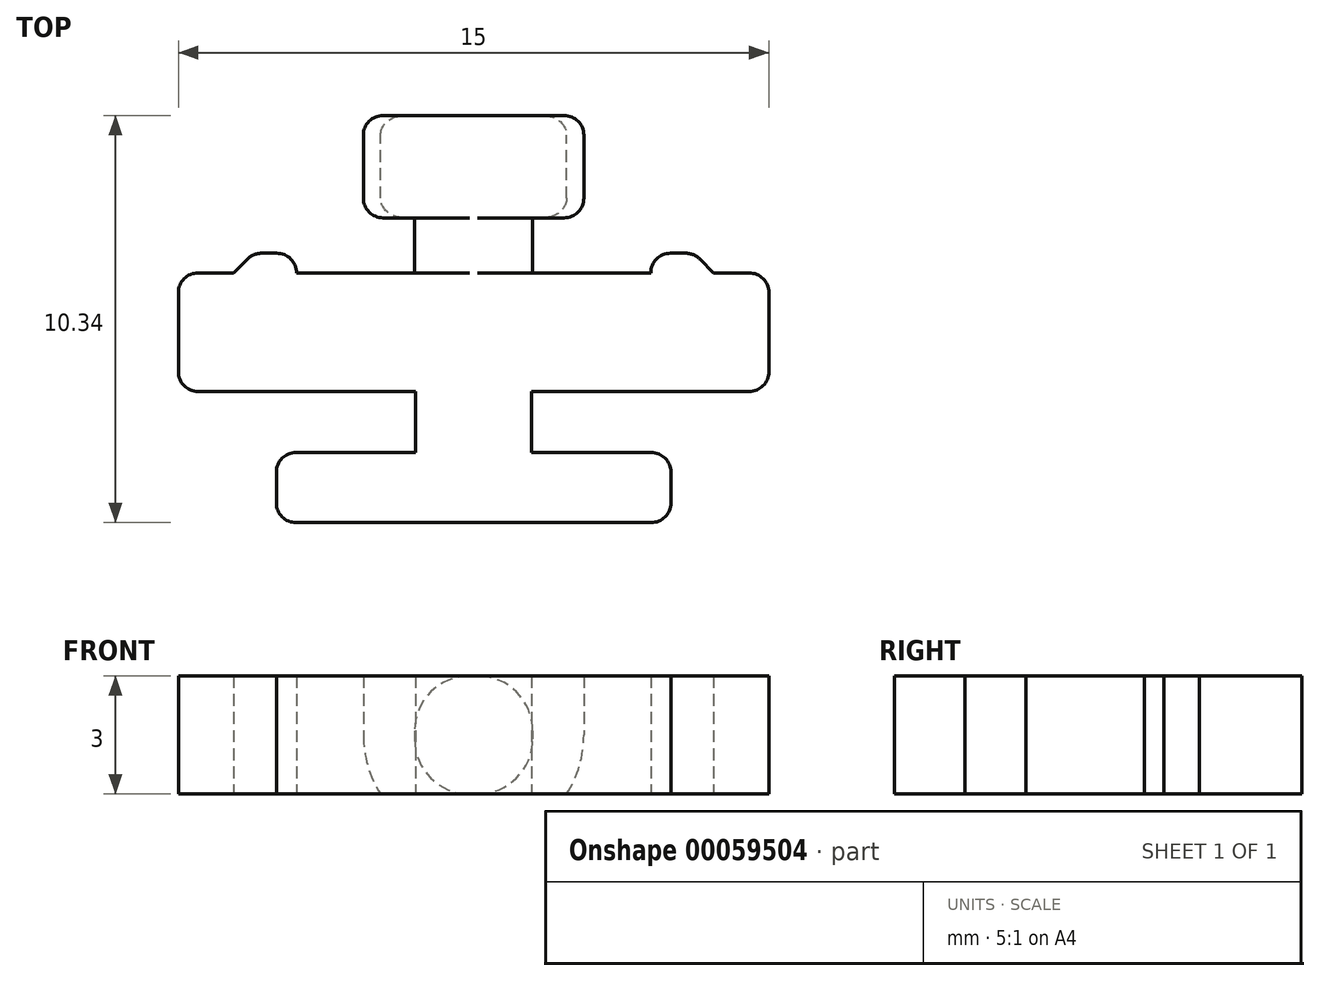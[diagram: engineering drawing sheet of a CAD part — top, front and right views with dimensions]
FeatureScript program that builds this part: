
annotation { "Feature Type Name" : "Feature", "Feature Type Description" : "" }
export const myFeature = defineFeature(function(context is Context, id is Id, definition is map)
    precondition{}
    {
        {
            assignVariable(context, id + "F0", {"name" : "SlotW", "anyValue" : 3});
        }
        {
            var Q0;
            Q0=qCreatedBy(makeId("Top.planeOp"),FACE);
            var sketch = newSketch(context, id + "F1", { "sketchPlane" : qUnion([Q0])});
            skLineSegment(sketch, "E0", {"start": v(2.8, 4) * mm, "end": v(2.8, 1.4) * mm});
            skLineSegment(sketch, "E1", {"start": v(2.8, 1.4) * mm, "end": v(1.5, 1.4) * mm});
            skLineSegment(sketch, "E2", {"start": v(1.5, 1.4) * mm, "end": v(1.5, 0) * mm});
            skLineSegment(sketch, "E3", {"start": v(1.5, 0) * mm, "end": v(4.5, 0) * mm});
            skLineSegment(sketch, "E4", {"start": v(4.5, 0) * mm, "end": v(4.5, 0.5) * mm});
            skLineSegment(sketch, "E5", {"start": v(4.5, 0.5) * mm, "end": v(5.6, 0.5) * mm});
            skLineSegment(sketch, "E6", {"start": v(5.6, 0.5) * mm, "end": v(6.1, 0) * mm});
            skLineSegment(sketch, "E7", {"start": v(6.1, 0) * mm, "end": v(7.5, 0) * mm});
            skLineSegment(sketch, "E8", {"start": v(7.5, 0) * mm, "end": v(7.5, -3.01) * mm});
            skLineSegment(sketch, "E9", {"start": v(7.5, -3.01) * mm, "end": v(1.47, -3.01) * mm});
            skLineSegment(sketch, "E10", {"start": v(1.47, -3.01) * mm, "end": v(1.47, -4.56) * mm});
            skLineSegment(sketch, "E11", {"start": v(1.47, -4.56) * mm, "end": v(5.01, -4.56) * mm});
            skLineSegment(sketch, "E12", {"start": v(5.01, -4.56) * mm, "end": v(5.01, -6.34) * mm});
            skLineSegment(sketch, "E13.MirrorCS", {"start": v(-4.5, 0.5) * mm, "end": v(-5.6, 0.5) * mm});
            skLineSegment(sketch, "E14.MirrorCS", {"start": v(-2.8, 4) * mm, "end": v(-2.8, 1.4) * mm});
            skLineSegment(sketch, "E15.MirrorCS", {"start": v(-2.8, 1.4) * mm, "end": v(-1.5, 1.4) * mm});
            skLineSegment(sketch, "E16.MirrorCS", {"start": v(-5.01, -4.56) * mm, "end": v(-5.01, -6.34) * mm});
            skLineSegment(sketch, "E17.MirrorCS", {"start": v(-1.47, -4.56) * mm, "end": v(-5.01, -4.56) * mm});
            skLineSegment(sketch, "E18.MirrorCS", {"start": v(-1.47, -3.01) * mm, "end": v(-1.47, -4.56) * mm});
            skLineSegment(sketch, "E19.MirrorCS", {"start": v(-1.5, 1.4) * mm, "end": v(-1.5, 0) * mm});
            skLineSegment(sketch, "E20.MirrorCS", {"start": v(-1.5, 0) * mm, "end": v(-4.5, 0) * mm});
            skLineSegment(sketch, "E21.MirrorCS", {"start": v(-5.6, 0.5) * mm, "end": v(-6.1, 0) * mm});
            skLineSegment(sketch, "E22.MirrorCS", {"start": v(-7.5, -3.01) * mm, "end": v(-1.47, -3.01) * mm});
            skLineSegment(sketch, "E23.MirrorCS", {"start": v(-6.1, 0) * mm, "end": v(-7.5, 0) * mm});
            skLineSegment(sketch, "E24.MirrorCS", {"start": v(-7.5, 0) * mm, "end": v(-7.5, -3.01) * mm});
            skLineSegment(sketch, "E25.MirrorCS", {"start": v(-4.5, 0) * mm, "end": v(-4.5, 0.5) * mm});
            skLineSegment(sketch, "E26", {"start": v(-2.8, 4) * mm, "end": v(2.8, 4) * mm});
            skLineSegment(sketch, "E27", {"start": v(-5.01, -6.34) * mm, "end": v(5.01, -6.34) * mm});
            skSolve(sketch);
        }
        {
            var Q0;
            Q0=makeQuery(id+"F1.imprint","IMPRINT",FACE,{"disambiguationData":[TD([[makeQuery(id+"F1.imprint","IMPRINT",EDGE,{"derivedFrom":sQuery(id+"F1.wireOp",EDGE,"E0")}),-1.0]])]});
            extrude(context, id + "F2", {"entities" : qUnion([Q0]), "depth" : (getVariable(context, 'SlotW')) * mm});
        }
        {
            var Q0;
            Q0=makeQuery(id+"F2.opExtrude","SWEPT_FACE",FACE,{"disambiguationData":[OSD([sQuery(id+"F1.wireOp",EDGE,"E26")])]});
            var sketch = newSketch(context, id + "F3", { "sketchPlane" : qUnion([Q0])});
            skCircle(sketch, "E28", {"center": v(0, 1.5) * mm, "radius": 2.8 * mm});
            skPoint(sketch, "E28.centerSnap0", {"position": v(2.8, 1.5) * mm});
            skSolve(sketch);
        }
        {
            var Q0;
            {var subQ0=sQuery(id+"F3.wireOp",EDGE,"E28");var subQ1=sQuery(id+"F1.wireOp",EDGE,"E26");var subQ2=makeQuery(id+"F2.opExtrude","CAP_EDGE",EDGE,{"disambiguationData":[OSD([subQ1])],"isStart":false});var subQ3=makeQuery(id+"F3.imprint","INTERSECT",VERTEX,{"disambiguationData":[OD(1.0)],"derivedFrom":[subQ2,subQ0]});Q0=makeQuery(id+"F3.imprint","IMPRINT",FACE,{"disambiguationData":[TD([[makeQuery(id+"F3.imprint","IMPRINT",EDGE,{"disambiguationData":[TD([[subQ3,-1.0]])],"derivedFrom":subQ0}),-1.0]])]});}
            var Q1;
            {var subQ0=sQuery(id+"F3.wireOp",EDGE,"E28");var subQ1=sQuery(id+"F1.wireOp",EDGE,"E26");var subQ2=makeQuery(id+"F2.opExtrude","CAP_EDGE",EDGE,{"disambiguationData":[OSD([subQ1])],"isStart":false});var subQ3=makeQuery(id+"F3.imprint","INTERSECT",VERTEX,{"disambiguationData":[OD(0.0)],"derivedFrom":[subQ2,subQ0]});Q1=makeQuery(id+"F3.imprint","IMPRINT",FACE,{"disambiguationData":[TD([[makeQuery(id+"F3.imprint","IMPRINT",EDGE,{"disambiguationData":[TD([[subQ3,1.0]])],"derivedFrom":subQ0}),-1.0]])]});}
            var Q2;
            {var subQ0=sQuery(id+"F3.wireOp",EDGE,"E28");var subQ1=sQuery(id+"F1.wireOp",EDGE,"E26");var subQ4=makeQuery(id+"F2.opExtrude","CAP_EDGE",EDGE,{"disambiguationData":[OSD([subQ1])],"isStart":true});var subQ5=makeQuery(id+"F3.imprint","INTERSECT",VERTEX,{"disambiguationData":[OD(1.0)],"derivedFrom":[subQ4,subQ0]});Q2=makeQuery(id+"F3.imprint","IMPRINT",FACE,{"disambiguationData":[TD([[makeQuery(id+"F3.imprint","IMPRINT",EDGE,{"disambiguationData":[TD([[subQ5,-1.0]])],"derivedFrom":subQ0}),-1.0]])]});}
            var Q3;
            {var subQ0=sQuery(id+"F3.wireOp",EDGE,"E28");var subQ1=sQuery(id+"F1.wireOp",EDGE,"E26");var subQ4=makeQuery(id+"F2.opExtrude","CAP_EDGE",EDGE,{"disambiguationData":[OSD([subQ1])],"isStart":true});var subQ5=makeQuery(id+"F3.imprint","INTERSECT",VERTEX,{"disambiguationData":[OD(0.0)],"derivedFrom":[subQ4,subQ0]});Q3=makeQuery(id+"F3.imprint","IMPRINT",FACE,{"disambiguationData":[TD([[makeQuery(id+"F3.imprint","IMPRINT",EDGE,{"disambiguationData":[TD([[subQ5,1.0]])],"derivedFrom":subQ0}),-1.0]])]});}
            extrude(context, id + "F4", {"entities" : qUnion([Q0, Q1, Q2, Q3]), "operationType" : NewBodyOperationType.REMOVE, "endBound" : BoundingType.UP_TO_NEXT, "oppositeDirection" : true, "depth" : 25 * mm});
        }
        {
            var Q0;
            Q0=makeQuery(id+"F2.opExtrude","SWEPT_EDGE",EDGE,{"disambiguationData":[OSD([sQuery(id+"F1.wireOp",EDGE,"E0"),sQuery(id+"F1.wireOp",EDGE,"E26")])]});
            var Q1;
            Q1=makeQuery(id+"F2.opExtrude","SWEPT_EDGE",EDGE,{"disambiguationData":[OSD([sQuery(id+"F1.wireOp",EDGE,"E14.MirrorCS"),sQuery(id+"F1.wireOp",EDGE,"E26")])]});
            var Q2;
            Q2=makeQuery(id+"F2.opExtrude","SWEPT_EDGE",EDGE,{"disambiguationData":[OSD([sQuery(id+"F1.wireOp",EDGE,"E4"),sQuery(id+"F1.wireOp",EDGE,"E5")])]});
            var Q3;
            Q3=makeQuery(id+"F2.opExtrude","SWEPT_EDGE",EDGE,{"disambiguationData":[OSD([sQuery(id+"F1.wireOp",EDGE,"E5"),sQuery(id+"F1.wireOp",EDGE,"E6")])]});
            var Q4;
            Q4=makeQuery(id+"F2.opExtrude","SWEPT_EDGE",EDGE,{"disambiguationData":[OSD([sQuery(id+"F1.wireOp",EDGE,"E7"),sQuery(id+"F1.wireOp",EDGE,"E8")])]});
            var Q5;
            Q5=makeQuery(id+"F2.opExtrude","SWEPT_EDGE",EDGE,{"disambiguationData":[OSD([sQuery(id+"F1.wireOp",EDGE,"E8"),sQuery(id+"F1.wireOp",EDGE,"E9")])]});
            var Q6;
            Q6=makeQuery(id+"F2.opExtrude","SWEPT_EDGE",EDGE,{"disambiguationData":[OSD([sQuery(id+"F1.wireOp",EDGE,"E11"),sQuery(id+"F1.wireOp",EDGE,"E12")])]});
            var Q7;
            Q7=makeQuery(id+"F2.opExtrude","SWEPT_EDGE",EDGE,{"disambiguationData":[OSD([sQuery(id+"F1.wireOp",EDGE,"E12"),sQuery(id+"F1.wireOp",EDGE,"E27")])]});
            var Q8;
            Q8=makeQuery(id+"F2.opExtrude","SWEPT_EDGE",EDGE,{"disambiguationData":[OSD([sQuery(id+"F1.wireOp",EDGE,"E0"),sQuery(id+"F1.wireOp",EDGE,"E1")])]});
            var Q9;
            Q9=makeQuery(id+"F2.opExtrude","SWEPT_EDGE",EDGE,{"disambiguationData":[OSD([sQuery(id+"F1.wireOp",EDGE,"E14.MirrorCS"),sQuery(id+"F1.wireOp",EDGE,"E15.MirrorCS")])]});
            var Q10;
            Q10=makeQuery(id+"F2.opExtrude","SWEPT_EDGE",EDGE,{"disambiguationData":[OSD([sQuery(id+"F1.wireOp",EDGE,"E13.MirrorCS"),sQuery(id+"F1.wireOp",EDGE,"E25.MirrorCS")])]});
            var Q11;
            Q11=makeQuery(id+"F2.opExtrude","SWEPT_EDGE",EDGE,{"disambiguationData":[OSD([sQuery(id+"F1.wireOp",EDGE,"E13.MirrorCS"),sQuery(id+"F1.wireOp",EDGE,"E21.MirrorCS")])]});
            var Q12;
            Q12=makeQuery(id+"F2.opExtrude","SWEPT_EDGE",EDGE,{"disambiguationData":[OSD([sQuery(id+"F1.wireOp",EDGE,"E23.MirrorCS"),sQuery(id+"F1.wireOp",EDGE,"E24.MirrorCS")])]});
            var Q13;
            Q13=makeQuery(id+"F2.opExtrude","SWEPT_EDGE",EDGE,{"disambiguationData":[OSD([sQuery(id+"F1.wireOp",EDGE,"E22.MirrorCS"),sQuery(id+"F1.wireOp",EDGE,"E24.MirrorCS")])]});
            var Q14;
            Q14=makeQuery(id+"F2.opExtrude","SWEPT_EDGE",EDGE,{"disambiguationData":[OSD([sQuery(id+"F1.wireOp",EDGE,"E16.MirrorCS"),sQuery(id+"F1.wireOp",EDGE,"E27")])]});
            var Q15;
            Q15=makeQuery(id+"F2.opExtrude","SWEPT_EDGE",EDGE,{"disambiguationData":[OSD([sQuery(id+"F1.wireOp",EDGE,"E16.MirrorCS"),sQuery(id+"F1.wireOp",EDGE,"E17.MirrorCS")])]});
            var Q16;
            {var subQ0=sQuery(id+"F3.wireOp",EDGE,"E28");var subQ1=sQuery(id+"F1.wireOp",EDGE,"E26");Q16=makeQuery(id+"F4.boolean.opBoolean","COPY",EDGE,{"derivedFrom":makeQuery(id+"F4.opExtrude","SWEPT_EDGE",EDGE,{"disambiguationData":[OSD([subQ1,subQ0]),TDD([makeQuery(id+"F3.imprint","INTERSECT",VERTEX,{"disambiguationData":[OD(1.0)],"derivedFrom":[makeQuery(id+"F2.opExtrude","CAP_EDGE",EDGE,{"disambiguationData":[OSD([subQ1])],"isStart":false}),subQ0]})])]})});}
            var Q17;
            {var subQ0=sQuery(id+"F3.wireOp",EDGE,"E28");var subQ1=sQuery(id+"F1.wireOp",EDGE,"E26");Q17=makeQuery(id+"F4.boolean.opBoolean","COPY",EDGE,{"derivedFrom":makeQuery(id+"F4.opExtrude","SWEPT_EDGE",EDGE,{"disambiguationData":[OSD([subQ1,subQ0]),TDD([makeQuery(id+"F3.imprint","INTERSECT",VERTEX,{"disambiguationData":[OD(0.0)],"derivedFrom":[makeQuery(id+"F2.opExtrude","CAP_EDGE",EDGE,{"disambiguationData":[OSD([subQ1])],"isStart":false}),subQ0]})])]})});}
            var Q18;
            {var subQ0=sQuery(id+"F3.wireOp",EDGE,"E28");var subQ1=sQuery(id+"F1.wireOp",EDGE,"E26");Q18=makeQuery(id+"F4.boolean.opBoolean","COPY",EDGE,{"derivedFrom":makeQuery(id+"F4.opExtrude","SWEPT_EDGE",EDGE,{"disambiguationData":[OSD([subQ1,subQ0]),TDD([makeQuery(id+"F3.imprint","INTERSECT",VERTEX,{"disambiguationData":[OD(1.0)],"derivedFrom":[makeQuery(id+"F2.opExtrude","CAP_EDGE",EDGE,{"disambiguationData":[OSD([subQ1])],"isStart":true}),subQ0]})])]})});}
            var Q19;
            {var subQ0=sQuery(id+"F3.wireOp",EDGE,"E28");var subQ1=sQuery(id+"F1.wireOp",EDGE,"E26");Q19=makeQuery(id+"F4.boolean.opBoolean","COPY",EDGE,{"derivedFrom":makeQuery(id+"F4.opExtrude","SWEPT_EDGE",EDGE,{"disambiguationData":[OSD([subQ1,subQ0]),TDD([makeQuery(id+"F3.imprint","INTERSECT",VERTEX,{"disambiguationData":[OD(0.0)],"derivedFrom":[makeQuery(id+"F2.opExtrude","CAP_EDGE",EDGE,{"disambiguationData":[OSD([subQ1])],"isStart":true}),subQ0]})])]})});}
            fillet(context, id + "F5", {"entities" : qUnion([Q0, Q1, Q2, Q3, Q4, Q5, Q6, Q7, Q8, Q9, Q10, Q11, Q12, Q13, Q14, Q15, Q16, Q17, Q18, Q19]), "radius" : .5 * mm, "tangentPropagation" : true, "allowEdgeOverflow" : false});
        }
        {
            var Q0;
            Q0=makeQuery(id+"F2.opExtrude","CAP_EDGE",EDGE,{"disambiguationData":[OSD([sQuery(id+"F1.wireOp",EDGE,"E2")])],"isStart":false});
            var Q1;
            Q1=makeQuery(id+"F2.opExtrude","CAP_EDGE",EDGE,{"disambiguationData":[OSD([sQuery(id+"F1.wireOp",EDGE,"E19.MirrorCS")])],"isStart":false});
            var Q2;
            Q2=makeQuery(id+"F2.opExtrude","CAP_EDGE",EDGE,{"disambiguationData":[OSD([sQuery(id+"F1.wireOp",EDGE,"E2")])],"isStart":true});
            var Q3;
            Q3=makeQuery(id+"F2.opExtrude","CAP_EDGE",EDGE,{"disambiguationData":[OSD([sQuery(id+"F1.wireOp",EDGE,"E19.MirrorCS")])],"isStart":true});
            fillet(context, id + "F6", {"entities" : qUnion([Q0, Q1, Q2, Q3]), "radius" : (getVariable(context, 'SlotW') / 2 - 0.1) * mm, "allowEdgeOverflow" : false});
        }
    });
